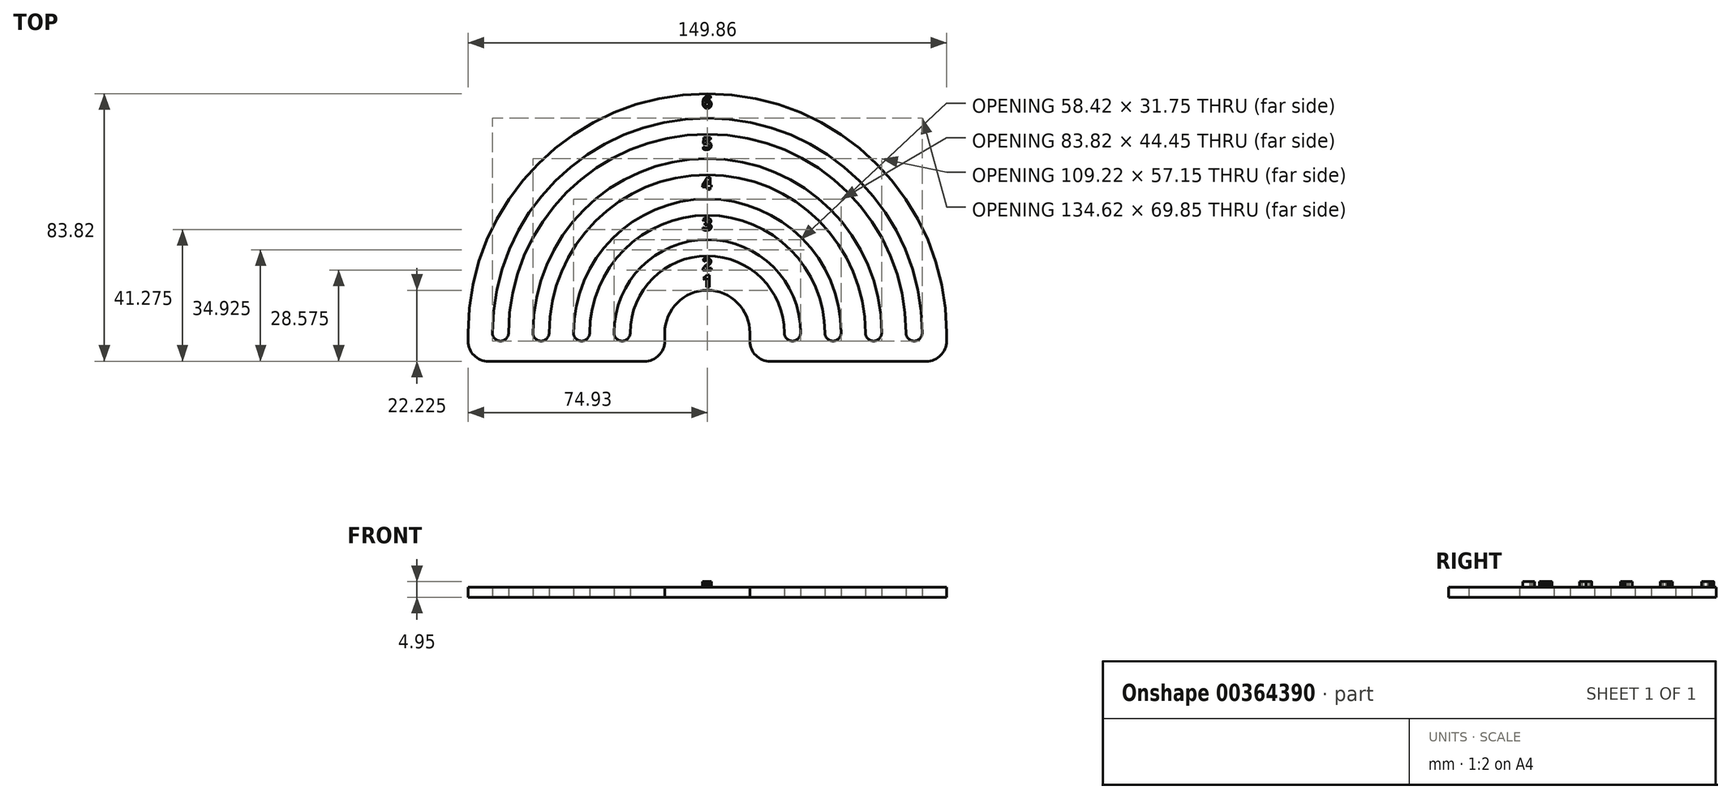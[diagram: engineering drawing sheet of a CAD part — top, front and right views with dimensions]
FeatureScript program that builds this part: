
annotation { "Feature Type Name" : "Feature", "Feature Type Description" : "" }
export const myFeature = defineFeature(function(context is Context, id is Id, definition is map)
    precondition{}
    {
        {
            var Q0;
            Q0=qCreatedBy(makeId("Top.planeOp"),FACE);
            var sketch = newSketch(context, id + "F0", { "sketchPlane" : qUnion([Q0])});
            skArc(sketch, "E0", {"start": v(74.93, 0) * mm, "mid": v(0, 74.93) * mm, "end": v(-74.93, 0) * mm});
            skArc(sketch, "E1", {"start": v(62.23, 0) * mm, "mid": v(0, 62.23) * mm, "end": v(-62.23, 0) * mm});
            skArc(sketch, "E2", {"start": v(49.53, 0) * mm, "mid": v(0, 49.53) * mm, "end": v(-49.53, 0) * mm});
            skArc(sketch, "E3", {"start": v(36.83, 0) * mm, "mid": v(0, 36.83) * mm, "end": v(-36.83, 0) * mm});
            skArc(sketch, "E4", {"start": v(24.13, 0) * mm, "mid": v(0, 24.13) * mm, "end": v(-24.13, 0) * mm});
            skArc(sketch, "E5", {"start": v(13.34, 0) * mm, "mid": v(0, 13.34) * mm, "end": v(-13.34, 0) * mm});
            skLineSegment(sketch, "E6", {"start": v(-102.54, 0) * mm, "end": v(119.68, 0) * mm, "construction": true});
            skArc(sketch, "E7.0", {"start": v(67.31, 0) * mm, "mid": v(0, 67.31) * mm, "end": v(-67.31, 0) * mm});
            skArc(sketch, "E8.0", {"start": v(54.61, 0) * mm, "mid": v(0, 54.61) * mm, "end": v(-54.61, 0) * mm});
            skArc(sketch, "E9.0", {"start": v(41.91, 0) * mm, "mid": v(0, 41.91) * mm, "end": v(-41.91, 0) * mm});
            skArc(sketch, "E10.0", {"start": v(29.21, 0) * mm, "mid": v(0, 29.21) * mm, "end": v(-29.21, 0) * mm});
            skArc(sketch, "E11", {"start": v(-67.31, 0) * mm, "mid": v(-64.77, -2.54) * mm, "end": v(-62.23, 0) * mm});
            skArc(sketch, "E12", {"start": v(-54.61, 0) * mm, "mid": v(-52.07, -2.54) * mm, "end": v(-49.53, 0) * mm});
            skArc(sketch, "E13", {"start": v(-41.91, 0) * mm, "mid": v(-39.37, -2.54) * mm, "end": v(-36.83, 0) * mm});
            skArc(sketch, "E14", {"start": v(-29.21, 0) * mm, "mid": v(-26.67, -2.54) * mm, "end": v(-24.13, 0) * mm});
            skArc(sketch, "E15.MirrorCS", {"start": v(29.21, 0) * mm, "mid": v(26.67, -2.54) * mm, "end": v(24.13, 0) * mm});
            skArc(sketch, "E16.MirrorCS", {"start": v(41.91, 0) * mm, "mid": v(39.37, -2.54) * mm, "end": v(36.83, 0) * mm});
            skArc(sketch, "E17.MirrorCS", {"start": v(54.61, 0) * mm, "mid": v(52.07, -2.54) * mm, "end": v(49.53, 0) * mm});
            skArc(sketch, "E18.MirrorCS", {"start": v(67.31, 0) * mm, "mid": v(64.77, -2.54) * mm, "end": v(62.23, 0) * mm});
            skLineSegment(sketch, "E19", {"start": v(-74.93, 0) * mm, "end": v(-74.93, -8.9) * mm});
            skLineSegment(sketch, "E20", {"start": v(74.93, 0) * mm, "end": v(74.93, -8.9) * mm});
            skLineSegment(sketch, "E21", {"start": v(-74.93, -8.9) * mm, "end": v(-13.34, -8.9) * mm});
            skLineSegment(sketch, "E22", {"start": v(-13.34, 0) * mm, "end": v(-13.34, -8.9) * mm});
            skLineSegment(sketch, "E23", {"start": v(13.34, 0) * mm, "end": v(13.34, -8.9) * mm});
            skLineSegment(sketch, "E24.trimOffspring", {"start": v(13.33, -8.9) * mm, "end": v(74.93, -8.9) * mm});
            skSolve(sketch);
        }
        {
            var Q0;
            Q0=makeQuery(id+"F0.imprint","IMPRINT",FACE,{"disambiguationData":[TD([[makeQuery(id+"F0.imprint","IMPRINT",EDGE,{"derivedFrom":sQuery(id+"F0.wireOp",EDGE,"E0")}),1.0]])]});
            extrude(context, id + "F1", {"entities" : qUnion([Q0]), "depth" : 3.17 * mm});
        }
        {
            var Q0;
            Q0=makeQuery(id+"F1.opExtrude","SWEPT_EDGE",EDGE,{"disambiguationData":[OSD([sQuery(id+"F0.wireOp",EDGE,"E19"),sQuery(id+"F0.wireOp",EDGE,"E21")])]});
            var Q1;
            Q1=makeQuery(id+"F1.opExtrude","SWEPT_EDGE",EDGE,{"disambiguationData":[OSD([sQuery(id+"F0.wireOp",EDGE,"E21"),sQuery(id+"F0.wireOp",EDGE,"E22")])]});
            var Q2;
            Q2=makeQuery(id+"F1.opExtrude","SWEPT_EDGE",EDGE,{"disambiguationData":[OSD([sQuery(id+"F0.wireOp",EDGE,"E23"),sQuery(id+"F0.wireOp",EDGE,"E24.trimOffspring")])]});
            var Q3;
            Q3=makeQuery(id+"F1.opExtrude","SWEPT_EDGE",EDGE,{"disambiguationData":[OSD([sQuery(id+"F0.wireOp",EDGE,"E20"),sQuery(id+"F0.wireOp",EDGE,"E24.trimOffspring")])]});
            fillet(context, id + "F2", {"entities" : qUnion([Q0, Q1, Q2, Q3]), "radius" : 6.35 * mm, "tangentPropagation" : true, "allowEdgeOverflow" : false});
        }
        {
            var Q0;
            Q0=makeQuery(id+"F1.opExtrude","CAP_FACE",FACE,{"disambiguationData":[OSD([sQuery(id+"F0.wireOp",EDGE,"E0"),sQuery(id+"F0.wireOp",EDGE,"E1"),sQuery(id+"F0.wireOp",EDGE,"E2"),sQuery(id+"F0.wireOp",EDGE,"E3"),sQuery(id+"F0.wireOp",EDGE,"E4"),sQuery(id+"F0.wireOp",EDGE,"E5"),sQuery(id+"F0.wireOp",EDGE,"E7.0"),sQuery(id+"F0.wireOp",EDGE,"E8.0"),sQuery(id+"F0.wireOp",EDGE,"E9.0"),sQuery(id+"F0.wireOp",EDGE,"E10.0"),sQuery(id+"F0.wireOp",EDGE,"E11"),sQuery(id+"F0.wireOp",EDGE,"E12"),sQuery(id+"F0.wireOp",EDGE,"E13"),sQuery(id+"F0.wireOp",EDGE,"E14"),sQuery(id+"F0.wireOp",EDGE,"E15.MirrorCS"),sQuery(id+"F0.wireOp",EDGE,"E16.MirrorCS"),sQuery(id+"F0.wireOp",EDGE,"E17.MirrorCS"),sQuery(id+"F0.wireOp",EDGE,"E18.MirrorCS"),sQuery(id+"F0.wireOp",EDGE,"E19"),sQuery(id+"F0.wireOp",EDGE,"E20"),sQuery(id+"F0.wireOp",EDGE,"E21"),sQuery(id+"F0.wireOp",EDGE,"E22"),sQuery(id+"F0.wireOp",EDGE,"E23"),sQuery(id+"F0.wireOp",EDGE,"E24.trimOffspring")])],"isStart":false});
            var sketch = newSketch(context, id + "F3", { "sketchPlane" : qUnion([Q0])});
            skText(sketch, "E25", { "text": "1", "fontName": "OpenSans-Bold.ttf"});
            skText(sketch, "E26", { "text": "2\n", "fontName": "OpenSans-Bold.ttf"});
            skText(sketch, "E27", { "text": "5", "fontName": "OpenSans-Bold.ttf"});
            skText(sketch, "E28", { "text": "4", "fontName": "OpenSans-Bold.ttf"});
            skText(sketch, "E29", { "text": "3", "fontName": "OpenSans-Bold.ttf"});
            skText(sketch, "E30", { "text": "6", "fontName": "OpenSans-Bold.ttf"});
            const initialGuessF3  = {"E25": [-0.00159, 0.01431, 1, 0, 0.0038], "E26": [-0.0016, 0.01962, 1, 0, 0.0038], "E27": [-0.00156, 0.05743, 1, 0, 0.00381], "E28": [-0.00164, 0.0449, 1, 0, 0.00381], "E29": [-0.00158, 0.03216, 1, 0, 0.00381], "E30": [-0.0016, 0.0704, 1, 0, 0.00381]};
            skSetInitialGuess(sketch, initialGuessF3);
            skSolve(sketch);
        }
        {
            var Q0;
            Q0 = qSketchRegion(id + "F3", true);
            extrude(context, id + "F4", {"entities" : qUnion([Q0]), "operationType" : NewBodyOperationType.ADD, "depth" : 1.78 * mm});
        }
    });
